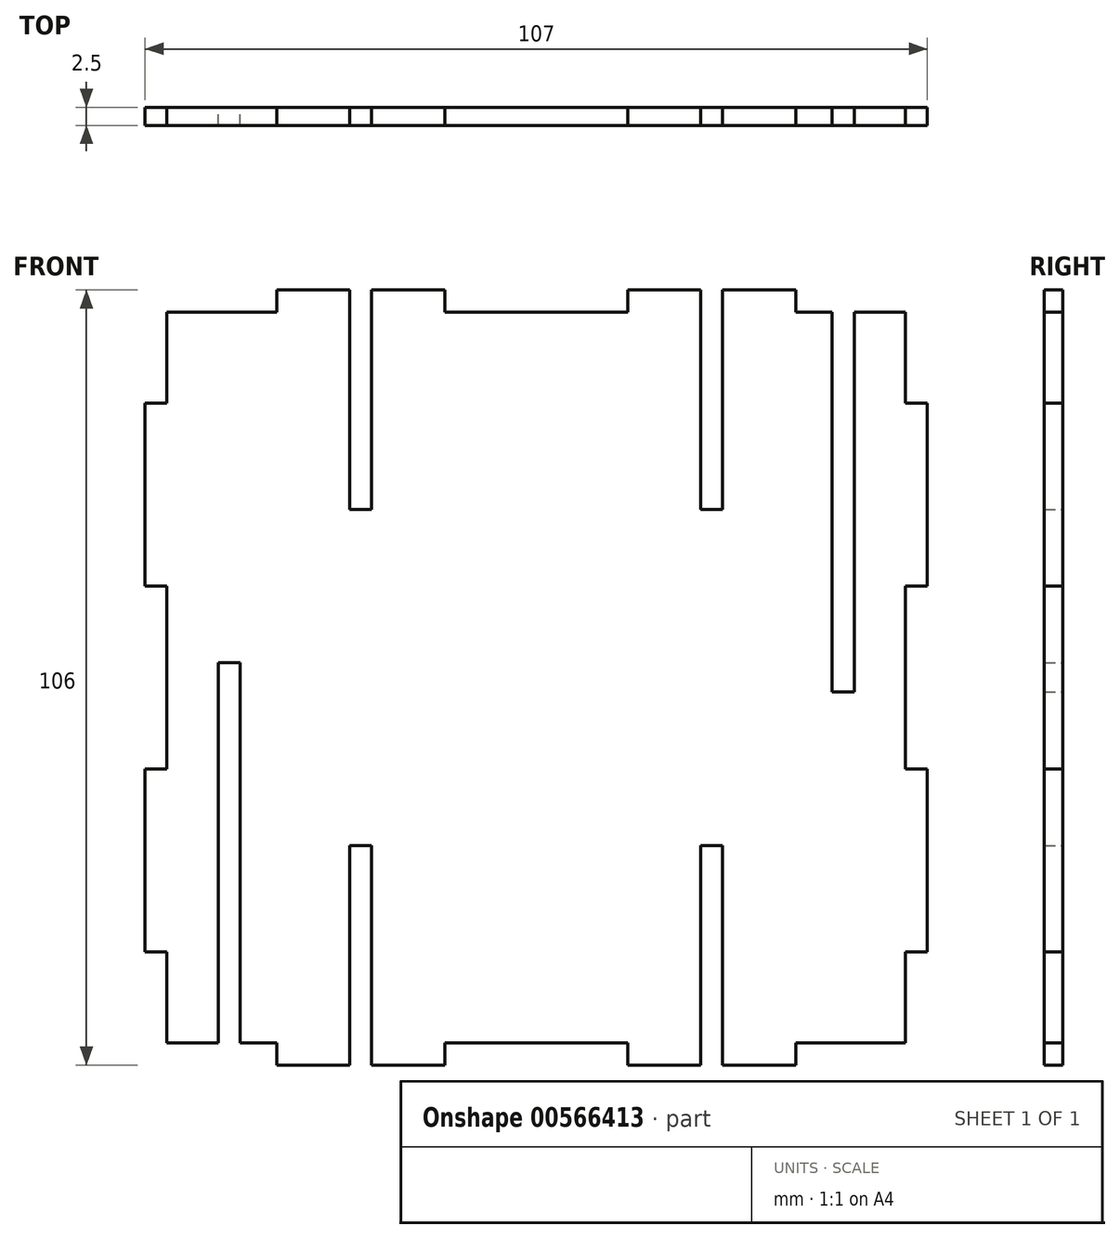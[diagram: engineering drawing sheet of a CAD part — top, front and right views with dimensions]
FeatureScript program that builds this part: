
annotation { "Feature Type Name" : "Feature", "Feature Type Description" : "" }
export const myFeature = defineFeature(function(context is Context, id is Id, definition is map)
    precondition{}
    {
        {
            var Q0;
            Q0=qCreatedBy(makeId("Front.planeOp"),FACE);
            var sketch = newSketch(context, id + "F0", { "sketchPlane" : qUnion([Q0])});
            skLineSegment(sketch, "E0", {"start": v(-64.71, -42.53) * mm, "end": v(-64.71, -30.03) * mm});
            skLineSegment(sketch, "E1", {"start": v(-64.71, -30.03) * mm, "end": v(-67.71, -30.03) * mm});
            skLineSegment(sketch, "E2", {"start": v(-67.71, -30.03) * mm, "end": v(-67.71, -5.03) * mm});
            skLineSegment(sketch, "E3", {"start": v(-67.71, -5.03) * mm, "end": v(-64.71, -5.03) * mm});
            skLineSegment(sketch, "E4", {"start": v(-64.71, -5.03) * mm, "end": v(-64.71, 19.97) * mm});
            skLineSegment(sketch, "E5", {"start": v(-64.71, 19.97) * mm, "end": v(-67.71, 19.97) * mm});
            skLineSegment(sketch, "E6", {"start": v(-67.71, 19.97) * mm, "end": v(-67.71, 44.97) * mm});
            skLineSegment(sketch, "E7", {"start": v(-67.71, 44.97) * mm, "end": v(-64.71, 44.97) * mm});
            skLineSegment(sketch, "E8", {"start": v(-64.71, 44.97) * mm, "end": v(-64.71, 57.47) * mm});
            skLineSegment(sketch, "E9", {"start": v(-64.71, 57.47) * mm, "end": v(-49.71, 57.47) * mm});
            skLineSegment(sketch, "E10", {"start": v(-49.71, 57.47) * mm, "end": v(-49.71, 60.47) * mm});
            skLineSegment(sketch, "E11", {"start": v(-49.71, 60.47) * mm, "end": v(-39.71, 60.47) * mm});
            skLineSegment(sketch, "E12", {"start": v(-39.71, 60.47) * mm, "end": v(-39.71, 30.47) * mm});
            skLineSegment(sketch, "E13", {"start": v(-39.71, 30.47) * mm, "end": v(-36.71, 30.47) * mm});
            skLineSegment(sketch, "E14", {"start": v(-36.71, 30.47) * mm, "end": v(-36.71, 60.47) * mm});
            skLineSegment(sketch, "E15", {"start": v(-36.71, 60.47) * mm, "end": v(-26.71, 60.47) * mm});
            skLineSegment(sketch, "E16", {"start": v(-26.71, 60.47) * mm, "end": v(-26.71, 57.47) * mm});
            skLineSegment(sketch, "E17", {"start": v(-26.71, 57.47) * mm, "end": v(-1.71, 57.47) * mm});
            skLineSegment(sketch, "E18", {"start": v(-1.71, 57.47) * mm, "end": v(-1.71, 60.47) * mm});
            skLineSegment(sketch, "E19", {"start": v(-1.71, 60.47) * mm, "end": v(8.29, 60.47) * mm});
            skLineSegment(sketch, "E20", {"start": v(8.29, 60.47) * mm, "end": v(8.29, 30.47) * mm});
            skLineSegment(sketch, "E21", {"start": v(8.29, 30.47) * mm, "end": v(11.29, 30.47) * mm});
            skLineSegment(sketch, "E22", {"start": v(11.29, 30.47) * mm, "end": v(11.29, 60.47) * mm});
            skLineSegment(sketch, "E23", {"start": v(11.29, 60.47) * mm, "end": v(21.29, 60.47) * mm});
            skLineSegment(sketch, "E24", {"start": v(21.29, 60.47) * mm, "end": v(21.29, 57.47) * mm});
            skLineSegment(sketch, "E25", {"start": v(26.29, 57.47) * mm, "end": v(26.29, 5.47) * mm});
            skLineSegment(sketch, "E26", {"start": v(26.29, 5.47) * mm, "end": v(29.29, 5.47) * mm});
            skLineSegment(sketch, "E27", {"start": v(29.29, 5.47) * mm, "end": v(29.29, 57.47) * mm});
            skLineSegment(sketch, "E28", {"start": v(29.29, 57.47) * mm, "end": v(36.29, 57.47) * mm});
            skLineSegment(sketch, "E29", {"start": v(21.29, 57.47) * mm, "end": v(26.29, 57.47) * mm});
            skLineSegment(sketch, "E30", {"start": v(36.29, 57.47) * mm, "end": v(36.29, 44.97) * mm});
            skLineSegment(sketch, "E31", {"start": v(36.29, 44.97) * mm, "end": v(39.29, 44.97) * mm});
            skLineSegment(sketch, "E32", {"start": v(39.29, 44.97) * mm, "end": v(39.29, 19.97) * mm});
            skLineSegment(sketch, "E33", {"start": v(39.29, 19.97) * mm, "end": v(36.29, 19.97) * mm});
            skLineSegment(sketch, "E34", {"start": v(36.29, 19.97) * mm, "end": v(36.29, -5.03) * mm});
            skLineSegment(sketch, "E35", {"start": v(36.29, -5.03) * mm, "end": v(39.29, -5.03) * mm});
            skLineSegment(sketch, "E36", {"start": v(39.29, -5.03) * mm, "end": v(39.29, -30.03) * mm});
            skLineSegment(sketch, "E37", {"start": v(39.29, -30.03) * mm, "end": v(36.29, -30.03) * mm});
            skLineSegment(sketch, "E38", {"start": v(36.29, -30.03) * mm, "end": v(36.29, -42.53) * mm});
            skLineSegment(sketch, "E39", {"start": v(36.29, -42.53) * mm, "end": v(21.29, -42.53) * mm});
            skLineSegment(sketch, "E40", {"start": v(21.29, -42.53) * mm, "end": v(21.29, -45.53) * mm});
            skLineSegment(sketch, "E41", {"start": v(21.29, -45.53) * mm, "end": v(11.29, -45.53) * mm});
            skLineSegment(sketch, "E42", {"start": v(11.29, -45.53) * mm, "end": v(11.29, -15.53) * mm});
            skLineSegment(sketch, "E43", {"start": v(11.29, -15.53) * mm, "end": v(8.29, -15.53) * mm});
            skLineSegment(sketch, "E44", {"start": v(8.29, -15.53) * mm, "end": v(8.29, -45.53) * mm});
            skLineSegment(sketch, "E45", {"start": v(8.29, -45.53) * mm, "end": v(-1.71, -45.53) * mm});
            skLineSegment(sketch, "E46", {"start": v(-1.71, -45.53) * mm, "end": v(-1.71, -42.53) * mm});
            skLineSegment(sketch, "E47", {"start": v(-1.71, -42.53) * mm, "end": v(-26.71, -42.53) * mm});
            skLineSegment(sketch, "E48", {"start": v(-26.71, -42.53) * mm, "end": v(-26.71, -45.53) * mm});
            skLineSegment(sketch, "E49", {"start": v(-26.71, -45.53) * mm, "end": v(-36.71, -45.53) * mm});
            skLineSegment(sketch, "E50", {"start": v(-36.71, -45.53) * mm, "end": v(-36.71, -15.53) * mm});
            skLineSegment(sketch, "E51", {"start": v(-36.71, -15.53) * mm, "end": v(-39.71, -15.53) * mm});
            skLineSegment(sketch, "E52", {"start": v(-39.71, -15.53) * mm, "end": v(-39.71, -45.53) * mm});
            skLineSegment(sketch, "E53", {"start": v(-39.71, -45.53) * mm, "end": v(-49.71, -45.53) * mm});
            skLineSegment(sketch, "E54", {"start": v(-49.71, -45.53) * mm, "end": v(-49.71, -42.53) * mm});
            skLineSegment(sketch, "E55", {"start": v(-49.71, -42.53) * mm, "end": v(-54.71, -42.53) * mm});
            skLineSegment(sketch, "E56", {"start": v(-54.71, -42.53) * mm, "end": v(-54.71, 9.47) * mm});
            skLineSegment(sketch, "E57", {"start": v(-54.71, 9.47) * mm, "end": v(-57.71, 9.47) * mm});
            skLineSegment(sketch, "E58", {"start": v(-57.71, 9.47) * mm, "end": v(-57.71, -42.53) * mm});
            skLineSegment(sketch, "E59", {"start": v(-57.71, -42.53) * mm, "end": v(-64.71, -42.53) * mm});
            skSolve(sketch);
        }
        {
            var Q0;
            Q0 = qSketchRegion(id + "F0", true);
            extrude(context, id + "F1", {"entities" : qUnion([Q0]), "depth" : 2.5 * mm, "offsetDistance" : 25 * mm});
        }
    });
